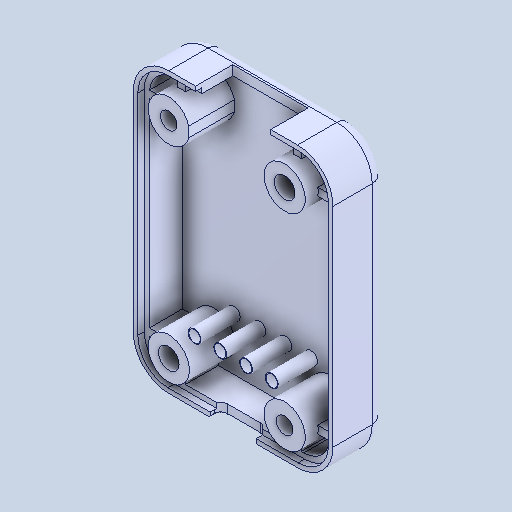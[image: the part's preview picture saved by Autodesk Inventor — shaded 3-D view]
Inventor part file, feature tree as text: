
AUTODESK INVENTOR PART (.ipt)
format: ipt  version: 2022.3 (Build 263350000, 350)  size: 322,048 bytes
history: native  units: in
note: dims shown in document units (in); Inventor stores cm internally (conversion verified against a paired STEP export)
features: fillet x1
ambient origin geometry x8: Origin, YZ Plane, XZ Plane, XY Plane, X Axis, Y Axis, Z Axis, Center Point
bodies: Solid1 (feature_tree)
feature tree (1):
  fillet  "Fillet11"  [1 undecoded]
note: 1 required parameter value undecoded (feature->parameter linkage not recoverable at this tier; creation-order binding heuristic only, values carry confidence <= 0.55)
